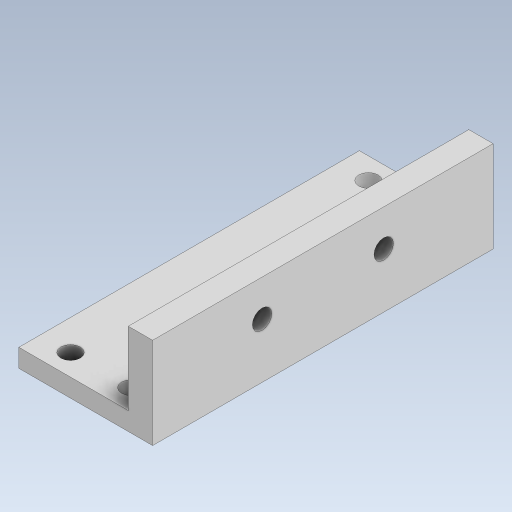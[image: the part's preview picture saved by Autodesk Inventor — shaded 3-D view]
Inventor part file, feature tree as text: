
AUTODESK INVENTOR PART (.ipt)
format: ipt  version: 2023.5 (Build 275446000, 446)  size: 301,568 bytes
history: native  units: mm
features: extrude x3, sketch x2
ambient origin geometry x8: Origin, YZ Plane, XZ Plane, XY Plane, X Axis, Y Axis, Z Axis, Center Point
bodies: Solid1 (feature_tree)
feature tree (5):
  sketch  "Sketch1"  dims[d0=3.2mm d2=24.5mm]
  extrude  "Extrusion1"  Depth=24.5mm
  extrude  "Extrusion2"  Depth=3.0mm TaperAngle=0.0deg
  extrude  "Extrusion3"  Depth=10.0mm
  sketch  "Sketch2"  dims[d3=5.0mm d4=3.0mm d5=0.0mm d6=2.0mm d7=15.0mm d8=0.0mm d9=3.2mm d10=5.5mm d11=15.0mm d12=0.0mm d13=10.0mm d15=0.5mm d16=0.872665mm d17=0.5mm d18=0.872665mm]
